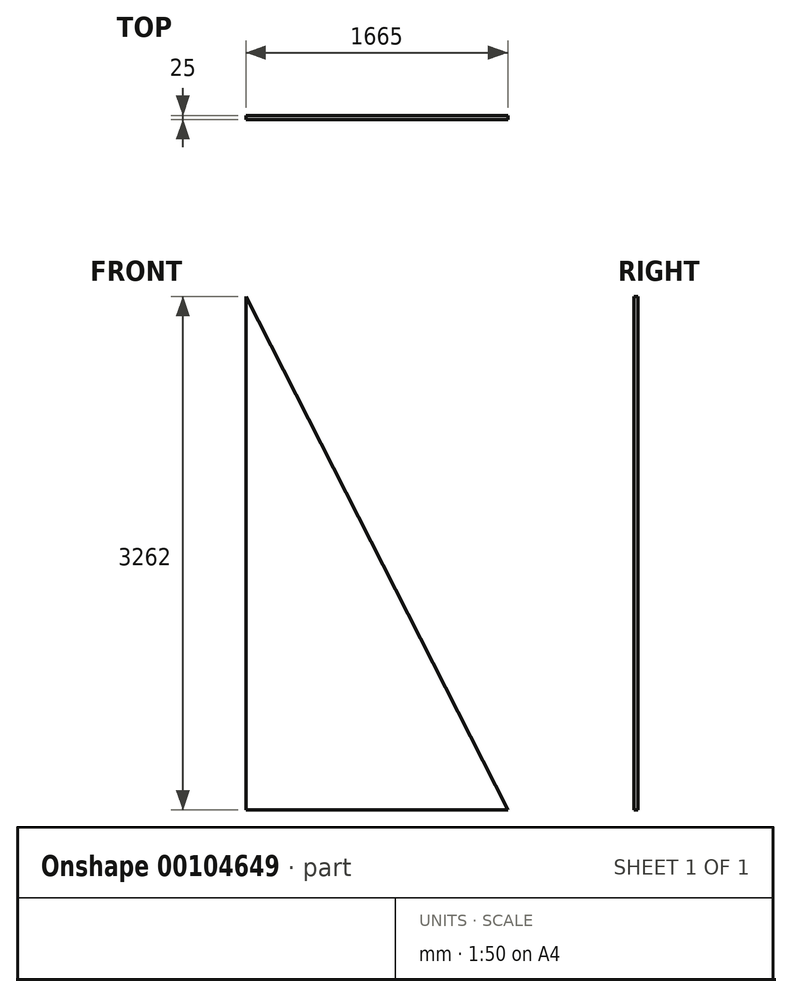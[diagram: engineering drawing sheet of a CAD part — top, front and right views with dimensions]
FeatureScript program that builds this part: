
annotation { "Feature Type Name" : "Feature", "Feature Type Description" : "" }
export const myFeature = defineFeature(function(context is Context, id is Id, definition is map)
    precondition{}
    {
        {
            var Q0;
            Q0=qCreatedBy(makeId("Front.planeOp"),FACE);
            var sketch = newSketch(context, id + "F0", { "sketchPlane" : qUnion([Q0])});
            skLineSegment(sketch, "E0", {"start": v(0, 0) * mm, "end": v(0, 3262) * mm});
            skLineSegment(sketch, "E1", {"start": v(0, 3262) * mm, "end": v(1665, 0) * mm});
            skLineSegment(sketch, "E2", {"start": v(1665, 0) * mm, "end": v(0, 0) * mm});
            skSolve(sketch);
        }
        {
            var Q0;
            Q0=makeQuery(id+"F0.imprint","IMPRINT",FACE,{"disambiguationData":[TD([[makeQuery(id+"F0.imprint","IMPRINT",EDGE,{"derivedFrom":sQuery(id+"F0.wireOp",EDGE,"E0")}),-1.0]])]});
            extrude(context, id + "F1", {"entities" : qUnion([Q0]), "oppositeDirection" : true, "depth" : 25 * mm});
        }
    });
